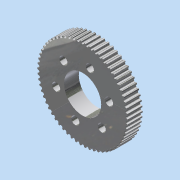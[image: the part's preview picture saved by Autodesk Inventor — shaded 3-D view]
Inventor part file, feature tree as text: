
AUTODESK INVENTOR PART (.ipt)
format: ipt  version: 2015 (Build 190159000, 159)  size: 1,550,336 bytes
history: native  units: in
note: dims shown in document units (in); Inventor stores cm internally (conversion verified against a paired STEP export)
features: projected_geometry x7, other x6, move_body x3, direct_edit x2, extrude x2, sketch x2, pattern_circular x1, split x1, chamfer x1, imported_body x1
ambient origin geometry x8: Origin, YZ Plane, XZ Plane, XY Plane, X Axis, Y Axis, Z Axis, Center Point
bodies: Solid1 (feature_tree)
feature tree (26):
  other  "WheelInsert.ipt"
  other  "a_6a22m062tm201"
  direct_edit  "Direct Edit1"
  direct_edit  "Direct Edit2"
  extrude  "Extrusion1"  Depth=0.1875in TaperAngle=0.0deg
  pattern_circular  "Circular Pattern1"  Count=62 Angle=360.0deg
  move_body  "Move Body1"
  split  "Split1"
  extrude  "Extrusion2"  Depth=0.3937in TaperAngle=360.0deg
  chamfer  "Chamfer1"  Distance=0.3937in
  imported_body  "Base1"
  sketch  "Sketch1"  dims[d0=0.0in d1=0.0in d2=0.1875in d3=0.0in d4=0.0in d5=0.1875in d6=24.4094in d8=360.0deg]
  projected_geometry  "Projected Loop1"
  other  "TaggingFeature1"
  sketch  "Sketch2"  dims[d10=0.3937in d11=0.0in d12=24.4094in d13=360.0deg d15=0.3937in d71=360.0deg d42=0.1625in d46=0.0in d47=0.375in d48=0.375in d49=0.375in d50=0.375in d51=0.375in d52=0.375in d53=0.01in d54=0.0in d67=0.01in d68=0.01in d69=2.3622in d73=0.02in d74=0.0in d78=0.047in d81=0.15in d82=0.145in d83=0.05in d84=0.0in d85=0.05in d89=0.0197in d90=0.0in d91=0.0197in d94=0.0098in d97=2.0in d98=2.3622in d99=360.0deg d16=90.0deg d17=0.0in d18=0.0in d19=-0.5866in d20=0.3937in d21=0.0in d22=0.9449in d23=0.0835in d24=0.0787in d25=45.0deg]
  projected_geometry  "Projected Loop2"
  projected_geometry  "Projected Loop3"
  projected_geometry  "Projected Loop4"
  projected_geometry  "Projected Loop5"
  projected_geometry  "Projected Loop6"
  projected_geometry  "Projected Loop7"
  other  "Delete1"
  move_body  "Move1"
  move_body  "Move2"
  other  "Solid1::WheelInsert.ipt"
  other  "Srf1"
